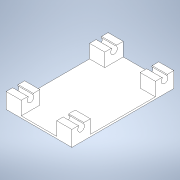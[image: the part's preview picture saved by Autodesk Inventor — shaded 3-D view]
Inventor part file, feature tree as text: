
AUTODESK INVENTOR PART (.ipt)
format: ipt  version: 2022 (Build 260153000, 153)  size: 235,520 bytes
history: native  units: in
note: dims shown in document units (in); Inventor stores cm internally (conversion verified against a paired STEP export)
features: extrude x13, sketch x13, mirror x2
ambient origin geometry x8: Origin, YZ Plane, XZ Plane, XY Plane, X Axis, Y Axis, Z Axis, Center Point
bodies: Solid1 (feature_tree)
feature tree (28):
  extrude  "Extrusion1"  Depth=23.8189in
  extrude  "Extrusion2"  Depth=4.3307in
  extrude  "Extrusion3"  Depth=3.5433in
  extrude  "Extrusion4"  Depth=3.1496in TaperAngle=0.0deg
  extrude  "Extrusion5"  Depth=0.748in
  mirror  "Mirror1"
  extrude  "Extrusion6"  Depth=1.5748in
  mirror  "Mirror2"
  extrude  "Extrusion7"  Depth=0.3937in
  extrude  "Extrusion8"  TaperAngle=45.0deg  [1 undecoded]
  extrude  "Extrusion9"  Depth=0.3937in
  extrude  "Extrusion10"  Depth=0.1969in
  extrude  "Extrusion11"  Depth=4.3307in TaperAngle=0.0deg
  extrude  "Extrusion12"  Depth=0.748in
  extrude  "Extrusion13"  Depth=4.3307in TaperAngle=0.0deg
  sketch  "Sketch1"  dims[d0=15.3543in d1=23.8189in]
  sketch  "Sketch2"  dims[d2=0.4724in d3=0.0in d4=4.3307in]
  sketch  "Sketch3"  dims[d5=90.0deg d6=3.5433in]
  sketch  "Sketch4"  dims[d7=90.0deg d8=3.1496in d9=0.0in]
  sketch  "Sketch5"  dims[d10=2.1654in d11=0.748in]
  sketch  "Sketch6"  dims[d12=90.0deg d13=1.5748in]
  sketch  "Sketch7"  dims[d14=4.3307in d15=0.0in d16=0.3937in]
  sketch  "Sketch8"  dims[d17=0.1969in d18=45.0deg]
  sketch  "Sketch9"  dims[d19=4.3307in d20=0.0in d21=0.3937in]
  sketch  "Sketch10"  dims[d22=0.0in d23=0.1969in]
  sketch  "Sketch11"  dims[d24=45.0deg d25=4.3307in d26=0.0in]
  sketch  "Sketch12"  dims[d27=2.1654in d28=0.748in]
  sketch  "Sketch13"  dims[d29=1.5748in d30=4.3307in d31=0.0in d32=4.3307in d33=0.0in d34=4.3307in d35=0.0in d36=0.3937in d37=45.0deg d38=4.3307in d39=0.0in d40=0.3937in d41=0.1969in d42=45.0deg d43=4.3307in d44=0.0in d45=0.3937in d46=0.1969in d47=45.0deg d48=4.3307in d49=0.0in d50=0.3937in d51=0.1969in d52=45.0deg d53=4.3307in d54=0.0in d55=0.3937in d56=0.1969in d57=45.0deg d58=0.3937in d59=0.1969in d60=45.0deg d61=4.3307in d62=0.0in]
note: 1 required parameter value undecoded (feature->parameter linkage not recoverable at this tier; creation-order binding heuristic only, values carry confidence <= 0.55)
